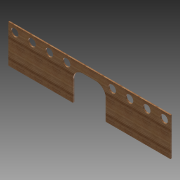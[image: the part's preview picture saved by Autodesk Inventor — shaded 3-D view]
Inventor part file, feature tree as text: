
AUTODESK INVENTOR PART (.ipt)
format: ipt  version: 2012 (Build 160160000, 160)  size: 115,200 bytes
history: native  units: in
note: dims shown in document units (in); Inventor stores cm internally (conversion verified against a paired STEP export)
features: extrude x1, sketch x1
ambient origin geometry x8: Origin, YZ Plane, XZ Plane, XY Plane, X Axis, Y Axis, Z Axis, Center Point
bodies: Solid1 (feature_tree)
feature tree (2):
  extrude  "Extrusion1"  Depth=32.0in
  sketch  "Sketch1"  dims[d0=7.5in d1=32.0in d11=0.25in d12=0.0in d13=1.5in d14=1.5in d15=9.0in d16=10.25in d17=3.4167in d18=3.4167in d19=1.25in d20=23.5in d21=1.25in d22=1.25in d23=1.25in d24=3.4167in d25=3.4167in d26=6.5in d28=12.75in d29=6.0in d30=2.0in]
